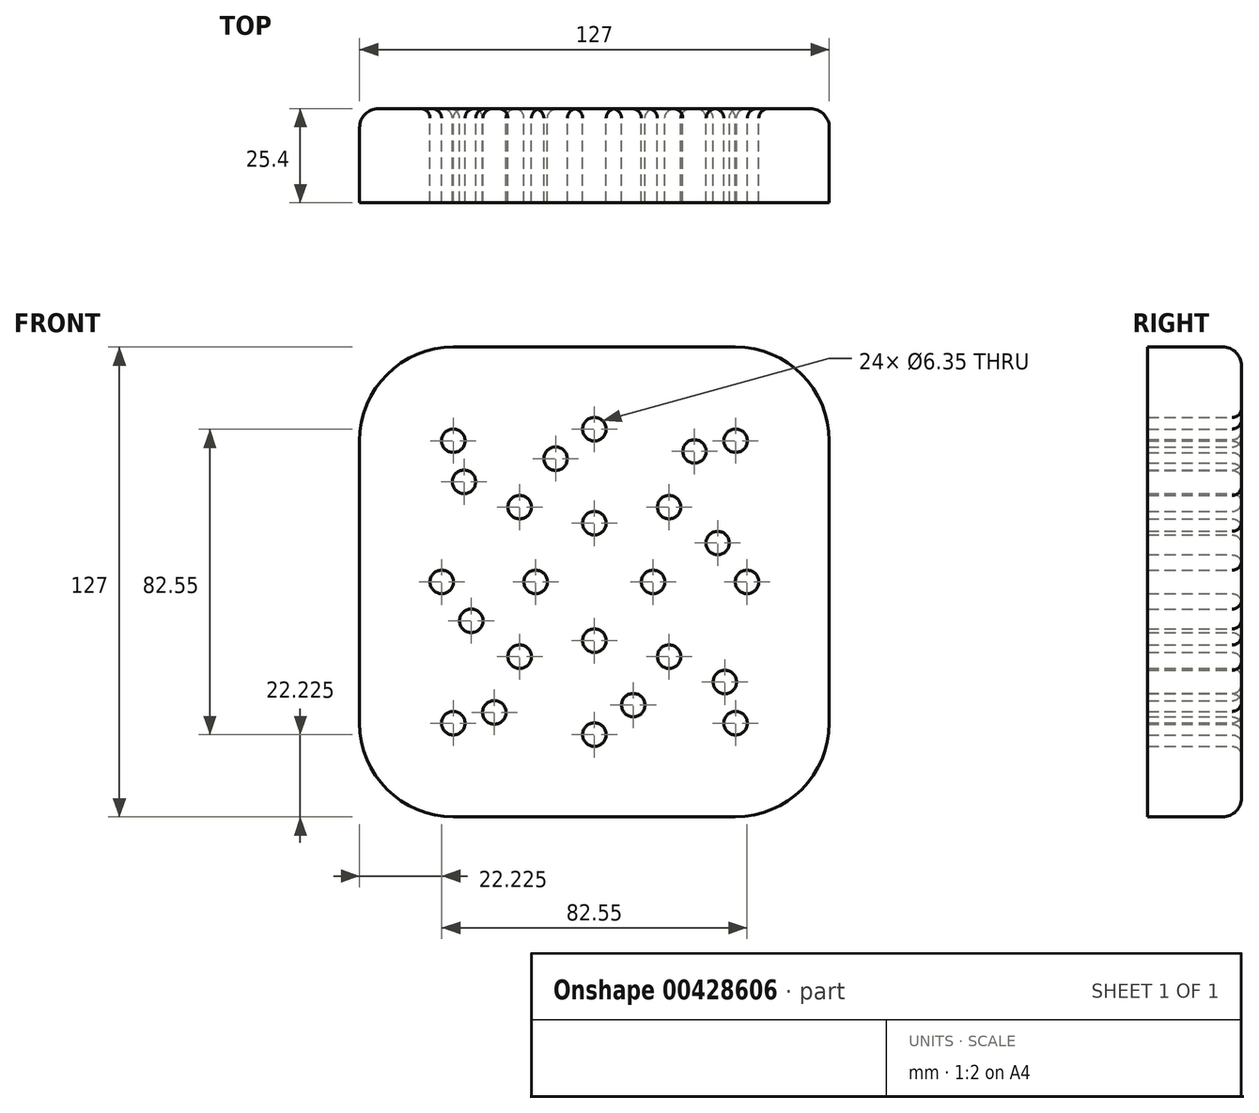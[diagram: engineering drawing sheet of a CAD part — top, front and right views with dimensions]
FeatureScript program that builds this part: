
annotation { "Feature Type Name" : "Feature", "Feature Type Description" : "" }
export const myFeature = defineFeature(function(context is Context, id is Id, definition is map)
    precondition{}
    {
        {
            var Q0;
            Q0=qCreatedBy(makeId("Front.planeOp"),FACE);
            var sketch = newSketch(context, id + "F0", { "sketchPlane" : qUnion([Q0])});
            skCircle(sketch, "E0", {"center": v(0, 0) * mm, "radius": 41.28 * mm, "construction": true});
            skCircle(sketch, "E1", {"center": v(0, -41.27) * mm, "radius": 3.18 * mm});
            skCircle(sketch, "E2", {"center": v(0, 41.28) * mm, "radius": 3.18 * mm});
            skCircle(sketch, "E3", {"center": v(41.27, 0) * mm, "radius": 3.18 * mm});
            skCircle(sketch, "E4", {"center": v(-41.27, 0) * mm, "radius": 3.18 * mm});
            skLineSegment(sketch, "E5", {"start": v(-41.28, 0) * mm, "end": v(0, -41.27) * mm, "construction": true});
            skLineSegment(sketch, "E6", {"start": v(0, -41.27) * mm, "end": v(41.28, 0) * mm, "construction": true});
            skLineSegment(sketch, "E7", {"start": v(41.28, 0) * mm, "end": v(0, 41.28) * mm, "construction": true});
            skLineSegment(sketch, "E8", {"start": v(0, 41.28) * mm, "end": v(-41.27, 0) * mm, "construction": true});
            skLineSegment(sketch, "E9.bottom", {"start": v(63.5, -63.5) * mm, "end": v(-63.5, -63.5) * mm});
            skLineSegment(sketch, "E9.top", {"start": v(63.5, 63.5) * mm, "end": v(-63.5, 63.5) * mm});
            skLineSegment(sketch, "E9.left", {"start": v(63.5, -63.5) * mm, "end": v(63.5, 63.5) * mm});
            skLineSegment(sketch, "E9.right", {"start": v(-63.5, -63.5) * mm, "end": v(-63.5, 63.5) * mm});
            skLineSegment(sketch, "E10", {"start": v(63.5, -63.5) * mm, "end": v(-63.5, 63.5) * mm, "construction": true});
            skLineSegment(sketch, "E11", {"start": v(63.5, 63.5) * mm, "end": v(-63.5, -63.5) * mm, "construction": true});
            skCircle(sketch, "E12", {"center": v(0, 0) * mm, "radius": 53.98 * mm, "construction": true});
            skCircle(sketch, "E13", {"center": v(-38.17, -38.17) * mm, "radius": 3.18 * mm});
            skCircle(sketch, "E14", {"center": v(-38.17, 38.17) * mm, "radius": 3.18 * mm});
            skCircle(sketch, "E15", {"center": v(38.17, 38.17) * mm, "radius": 3.18 * mm});
            skCircle(sketch, "E16", {"center": v(38.17, -38.17) * mm, "radius": 3.18 * mm});
            skLineSegment(sketch, "E17", {"start": v(-38.17, -38.17) * mm, "end": v(-38.17, 38.17) * mm, "construction": true});
            skLineSegment(sketch, "E18", {"start": v(-38.17, 38.17) * mm, "end": v(38.17, 38.17) * mm, "construction": true});
            skLineSegment(sketch, "E19", {"start": v(38.17, 38.17) * mm, "end": v(38.17, -38.17) * mm, "construction": true});
            skLineSegment(sketch, "E20", {"start": v(38.17, -38.17) * mm, "end": v(-38.17, -38.17) * mm, "construction": true});
            skCircle(sketch, "E21", {"center": v(0, 0) * mm, "radius": 28.58 * mm, "construction": true});
            skCircle(sketch, "E22", {"center": v(-20.2, -20.2) * mm, "radius": 3.18 * mm});
            skCircle(sketch, "E23", {"center": v(-20.2, 20.2) * mm, "radius": 3.18 * mm});
            skCircle(sketch, "E24", {"center": v(20.2, 20.2) * mm, "radius": 3.18 * mm});
            skCircle(sketch, "E25", {"center": v(20.2, -20.2) * mm, "radius": 3.18 * mm});
            skLineSegment(sketch, "E26", {"start": v(-20.2, -20.2) * mm, "end": v(-20.2, 20.2) * mm, "construction": true});
            skLineSegment(sketch, "E27", {"start": v(-20.2, 20.2) * mm, "end": v(20.2, 20.2) * mm, "construction": true});
            skLineSegment(sketch, "E28", {"start": v(20.2, 20.2) * mm, "end": v(20.2, -20.2) * mm, "construction": true});
            skLineSegment(sketch, "E29", {"start": v(20.2, -20.2) * mm, "end": v(-20.2, -20.2) * mm, "construction": true});
            skCircle(sketch, "E30", {"center": v(0, 0) * mm, "radius": 15.88 * mm, "construction": true});
            skCircle(sketch, "E31", {"center": v(0, -15.87) * mm, "radius": 3.18 * mm});
            skCircle(sketch, "E32", {"center": v(-15.88, 0) * mm, "radius": 3.17 * mm});
            skCircle(sketch, "E33", {"center": v(0, 15.88) * mm, "radius": 3.17 * mm});
            skCircle(sketch, "E34", {"center": v(15.88, 0) * mm, "radius": 3.17 * mm});
            skLineSegment(sketch, "E35", {"start": v(0, -15.87) * mm, "end": v(-15.88, 0) * mm, "construction": true});
            skLineSegment(sketch, "E36", {"start": v(-15.88, 0) * mm, "end": v(0, 15.88) * mm, "construction": true});
            skLineSegment(sketch, "E37", {"start": v(0, 15.88) * mm, "end": v(15.87, 0) * mm, "construction": true});
            skLineSegment(sketch, "E38", {"start": v(15.87, 0) * mm, "end": v(0, -15.88) * mm, "construction": true});
            skCircle(sketch, "E39", {"center": v(0, 0) * mm, "radius": 44.45 * mm, "construction": true});
            skCircle(sketch, "E40", {"center": v(-27.06, -35.26) * mm, "radius": 3.18 * mm});
            skCircle(sketch, "E41", {"center": v(-35.26, 27.06) * mm, "radius": 3.17 * mm});
            skCircle(sketch, "E42", {"center": v(27.06, 35.26) * mm, "radius": 3.17 * mm});
            skCircle(sketch, "E43", {"center": v(35.26, -27.06) * mm, "radius": 3.17 * mm});
            skLineSegment(sketch, "E44", {"start": v(-27.06, -35.26) * mm, "end": v(-35.26, 27.06) * mm, "construction": true});
            skLineSegment(sketch, "E45", {"start": v(-35.26, 27.06) * mm, "end": v(27.06, 35.26) * mm, "construction": true});
            skLineSegment(sketch, "E46", {"start": v(27.06, 35.26) * mm, "end": v(35.26, -27.06) * mm, "construction": true});
            skLineSegment(sketch, "E47", {"start": v(35.26, -27.06) * mm, "end": v(-27.06, -35.26) * mm, "construction": true});
            skCircle(sketch, "E48", {"center": v(0, 0) * mm, "radius": 34.93 * mm, "construction": true});
            skCircle(sketch, "E49", {"center": v(-33.3, -10.5) * mm, "radius": 3.18 * mm});
            skCircle(sketch, "E50", {"center": v(-10.5, 33.3) * mm, "radius": 3.17 * mm});
            skCircle(sketch, "E51", {"center": v(33.3, 10.5) * mm, "radius": 3.17 * mm});
            skCircle(sketch, "E52", {"center": v(10.5, -33.3) * mm, "radius": 3.17 * mm});
            skLineSegment(sketch, "E53", {"start": v(-33.3, -10.5) * mm, "end": v(-10.5, 33.3) * mm, "construction": true});
            skLineSegment(sketch, "E54", {"start": v(-10.5, 33.3) * mm, "end": v(33.3, 10.5) * mm, "construction": true});
            skLineSegment(sketch, "E55", {"start": v(33.3, 10.5) * mm, "end": v(10.5, -33.3) * mm, "construction": true});
            skLineSegment(sketch, "E56", {"start": v(10.5, -33.3) * mm, "end": v(-33.3, -10.5) * mm, "construction": true});
            skSolve(sketch);
        }
        {
            var Q0;
            Q0=makeQuery(id+"F0.imprint","IMPRINT",FACE,{"disambiguationData":[TD([[makeQuery(id+"F0.imprint","IMPRINT",EDGE,{"derivedFrom":sQuery(id+"F0.wireOp",EDGE,"E1")}),-1.0]])]});
            extrude(context, id + "F1", {"entities" : qUnion([Q0]), "depth" : 25.4 * mm});
        }
        {
            var Q0;
            Q0=makeQuery(id+"F1.opExtrude","SWEPT_EDGE",EDGE,{"disambiguationData":[OSD([sQuery(id+"F0.wireOp",EDGE,"E9.bottom"),sQuery(id+"F0.wireOp",EDGE,"E9.right")])]});
            var Q1;
            Q1=makeQuery(id+"F1.opExtrude","SWEPT_EDGE",EDGE,{"disambiguationData":[OSD([sQuery(id+"F0.wireOp",EDGE,"E9.top"),sQuery(id+"F0.wireOp",EDGE,"E9.right")])]});
            var Q2;
            Q2=makeQuery(id+"F1.opExtrude","SWEPT_EDGE",EDGE,{"disambiguationData":[OSD([sQuery(id+"F0.wireOp",EDGE,"E9.top"),sQuery(id+"F0.wireOp",EDGE,"E9.left")])]});
            var Q3;
            Q3=makeQuery(id+"F1.opExtrude","SWEPT_EDGE",EDGE,{"disambiguationData":[OSD([sQuery(id+"F0.wireOp",EDGE,"E9.bottom"),sQuery(id+"F0.wireOp",EDGE,"E9.left")])]});
            fillet(context, id + "F2", {"entities" : qUnion([Q0, Q1, Q2, Q3]), "radius" : 25.4 * mm, "tangentPropagation" : true, "allowEdgeOverflow" : false});
        }
        {
            var Q0;
            {var subQ0=sQuery(id+"F0.wireOp",EDGE,"E9.right");var subQ1=sQuery(id+"F0.wireOp",EDGE,"E9.bottom");Q0=makeQuery(id+"F2.opFillet","BLEND_EDGE",EDGE,{"blendedFrom":[makeQuery(id+"F1.opExtrude","SWEPT_EDGE",EDGE,{"disambiguationData":[OSD([subQ1,subQ0])]}),makeQuery(id+"F1.opExtrude","CAP_FACE",FACE,{"disambiguationData":[OSD([sQuery(id+"F0.wireOp",EDGE,"E1"),sQuery(id+"F0.wireOp",EDGE,"E2"),sQuery(id+"F0.wireOp",EDGE,"E3"),sQuery(id+"F0.wireOp",EDGE,"E4"),subQ1,sQuery(id+"F0.wireOp",EDGE,"E9.top"),sQuery(id+"F0.wireOp",EDGE,"E9.left"),subQ0,sQuery(id+"F0.wireOp",EDGE,"E13"),sQuery(id+"F0.wireOp",EDGE,"E14"),sQuery(id+"F0.wireOp",EDGE,"E15"),sQuery(id+"F0.wireOp",EDGE,"E16"),sQuery(id+"F0.wireOp",EDGE,"E22"),sQuery(id+"F0.wireOp",EDGE,"E23"),sQuery(id+"F0.wireOp",EDGE,"E24"),sQuery(id+"F0.wireOp",EDGE,"E25"),sQuery(id+"F0.wireOp",EDGE,"E31"),sQuery(id+"F0.wireOp",EDGE,"E32"),sQuery(id+"F0.wireOp",EDGE,"E33"),sQuery(id+"F0.wireOp",EDGE,"E34"),sQuery(id+"F0.wireOp",EDGE,"E40"),sQuery(id+"F0.wireOp",EDGE,"E41"),sQuery(id+"F0.wireOp",EDGE,"E42"),sQuery(id+"F0.wireOp",EDGE,"E43"),sQuery(id+"F0.wireOp",EDGE,"E49"),sQuery(id+"F0.wireOp",EDGE,"E50"),sQuery(id+"F0.wireOp",EDGE,"E51"),sQuery(id+"F0.wireOp",EDGE,"E52")])],"isStart":true})],"blendedInto":[makeQuery(id+"F1.opExtrude","CAP_FACE",FACE,{"disambiguationData":[OSD([sQuery(id+"F0.wireOp",EDGE,"E1"),sQuery(id+"F0.wireOp",EDGE,"E2"),sQuery(id+"F0.wireOp",EDGE,"E3"),sQuery(id+"F0.wireOp",EDGE,"E4"),subQ1,sQuery(id+"F0.wireOp",EDGE,"E9.top"),sQuery(id+"F0.wireOp",EDGE,"E9.left"),subQ0,sQuery(id+"F0.wireOp",EDGE,"E13"),sQuery(id+"F0.wireOp",EDGE,"E14"),sQuery(id+"F0.wireOp",EDGE,"E15"),sQuery(id+"F0.wireOp",EDGE,"E16"),sQuery(id+"F0.wireOp",EDGE,"E22"),sQuery(id+"F0.wireOp",EDGE,"E23"),sQuery(id+"F0.wireOp",EDGE,"E24"),sQuery(id+"F0.wireOp",EDGE,"E25"),sQuery(id+"F0.wireOp",EDGE,"E31"),sQuery(id+"F0.wireOp",EDGE,"E32"),sQuery(id+"F0.wireOp",EDGE,"E33"),sQuery(id+"F0.wireOp",EDGE,"E34"),sQuery(id+"F0.wireOp",EDGE,"E40"),sQuery(id+"F0.wireOp",EDGE,"E41"),sQuery(id+"F0.wireOp",EDGE,"E42"),sQuery(id+"F0.wireOp",EDGE,"E43"),sQuery(id+"F0.wireOp",EDGE,"E49"),sQuery(id+"F0.wireOp",EDGE,"E50"),sQuery(id+"F0.wireOp",EDGE,"E51"),sQuery(id+"F0.wireOp",EDGE,"E52")])],"isStart":true})]});}
            var Q1;
            Q1=makeQuery(id+"F1.opExtrude","CAP_EDGE",EDGE,{"disambiguationData":[OSD([sQuery(id+"F0.wireOp",EDGE,"E9.bottom")])],"isStart":true});
            var Q2;
            {var subQ0=sQuery(id+"F0.wireOp",EDGE,"E9.left");var subQ1=sQuery(id+"F0.wireOp",EDGE,"E9.bottom");Q2=makeQuery(id+"F2.opFillet","BLEND_EDGE",EDGE,{"blendedFrom":[makeQuery(id+"F1.opExtrude","SWEPT_EDGE",EDGE,{"disambiguationData":[OSD([subQ1,subQ0])]}),makeQuery(id+"F1.opExtrude","CAP_FACE",FACE,{"disambiguationData":[OSD([sQuery(id+"F0.wireOp",EDGE,"E1"),sQuery(id+"F0.wireOp",EDGE,"E2"),sQuery(id+"F0.wireOp",EDGE,"E3"),sQuery(id+"F0.wireOp",EDGE,"E4"),subQ1,sQuery(id+"F0.wireOp",EDGE,"E9.top"),subQ0,sQuery(id+"F0.wireOp",EDGE,"E9.right"),sQuery(id+"F0.wireOp",EDGE,"E13"),sQuery(id+"F0.wireOp",EDGE,"E14"),sQuery(id+"F0.wireOp",EDGE,"E15"),sQuery(id+"F0.wireOp",EDGE,"E16"),sQuery(id+"F0.wireOp",EDGE,"E22"),sQuery(id+"F0.wireOp",EDGE,"E23"),sQuery(id+"F0.wireOp",EDGE,"E24"),sQuery(id+"F0.wireOp",EDGE,"E25"),sQuery(id+"F0.wireOp",EDGE,"E31"),sQuery(id+"F0.wireOp",EDGE,"E32"),sQuery(id+"F0.wireOp",EDGE,"E33"),sQuery(id+"F0.wireOp",EDGE,"E34"),sQuery(id+"F0.wireOp",EDGE,"E40"),sQuery(id+"F0.wireOp",EDGE,"E41"),sQuery(id+"F0.wireOp",EDGE,"E42"),sQuery(id+"F0.wireOp",EDGE,"E43"),sQuery(id+"F0.wireOp",EDGE,"E49"),sQuery(id+"F0.wireOp",EDGE,"E50"),sQuery(id+"F0.wireOp",EDGE,"E51"),sQuery(id+"F0.wireOp",EDGE,"E52")])],"isStart":true})],"blendedInto":[makeQuery(id+"F1.opExtrude","CAP_FACE",FACE,{"disambiguationData":[OSD([sQuery(id+"F0.wireOp",EDGE,"E1"),sQuery(id+"F0.wireOp",EDGE,"E2"),sQuery(id+"F0.wireOp",EDGE,"E3"),sQuery(id+"F0.wireOp",EDGE,"E4"),subQ1,sQuery(id+"F0.wireOp",EDGE,"E9.top"),subQ0,sQuery(id+"F0.wireOp",EDGE,"E9.right"),sQuery(id+"F0.wireOp",EDGE,"E13"),sQuery(id+"F0.wireOp",EDGE,"E14"),sQuery(id+"F0.wireOp",EDGE,"E15"),sQuery(id+"F0.wireOp",EDGE,"E16"),sQuery(id+"F0.wireOp",EDGE,"E22"),sQuery(id+"F0.wireOp",EDGE,"E23"),sQuery(id+"F0.wireOp",EDGE,"E24"),sQuery(id+"F0.wireOp",EDGE,"E25"),sQuery(id+"F0.wireOp",EDGE,"E31"),sQuery(id+"F0.wireOp",EDGE,"E32"),sQuery(id+"F0.wireOp",EDGE,"E33"),sQuery(id+"F0.wireOp",EDGE,"E34"),sQuery(id+"F0.wireOp",EDGE,"E40"),sQuery(id+"F0.wireOp",EDGE,"E41"),sQuery(id+"F0.wireOp",EDGE,"E42"),sQuery(id+"F0.wireOp",EDGE,"E43"),sQuery(id+"F0.wireOp",EDGE,"E49"),sQuery(id+"F0.wireOp",EDGE,"E50"),sQuery(id+"F0.wireOp",EDGE,"E51"),sQuery(id+"F0.wireOp",EDGE,"E52")])],"isStart":true})]});}
            var Q3;
            Q3=makeQuery(id+"F1.opExtrude","CAP_EDGE",EDGE,{"disambiguationData":[OSD([sQuery(id+"F0.wireOp",EDGE,"E9.left")])],"isStart":true});
            var Q4;
            Q4=makeQuery(id+"F1.opExtrude","CAP_EDGE",EDGE,{"disambiguationData":[OSD([sQuery(id+"F0.wireOp",EDGE,"E9.right")])],"isStart":true});
            var Q5;
            {var subQ0=sQuery(id+"F0.wireOp",EDGE,"E9.right");var subQ1=sQuery(id+"F0.wireOp",EDGE,"E9.top");Q5=makeQuery(id+"F2.opFillet","BLEND_EDGE",EDGE,{"blendedFrom":[makeQuery(id+"F1.opExtrude","SWEPT_EDGE",EDGE,{"disambiguationData":[OSD([subQ1,subQ0])]}),makeQuery(id+"F1.opExtrude","CAP_FACE",FACE,{"disambiguationData":[OSD([sQuery(id+"F0.wireOp",EDGE,"E1"),sQuery(id+"F0.wireOp",EDGE,"E2"),sQuery(id+"F0.wireOp",EDGE,"E3"),sQuery(id+"F0.wireOp",EDGE,"E4"),sQuery(id+"F0.wireOp",EDGE,"E9.bottom"),subQ1,sQuery(id+"F0.wireOp",EDGE,"E9.left"),subQ0,sQuery(id+"F0.wireOp",EDGE,"E13"),sQuery(id+"F0.wireOp",EDGE,"E14"),sQuery(id+"F0.wireOp",EDGE,"E15"),sQuery(id+"F0.wireOp",EDGE,"E16"),sQuery(id+"F0.wireOp",EDGE,"E22"),sQuery(id+"F0.wireOp",EDGE,"E23"),sQuery(id+"F0.wireOp",EDGE,"E24"),sQuery(id+"F0.wireOp",EDGE,"E25"),sQuery(id+"F0.wireOp",EDGE,"E31"),sQuery(id+"F0.wireOp",EDGE,"E32"),sQuery(id+"F0.wireOp",EDGE,"E33"),sQuery(id+"F0.wireOp",EDGE,"E34"),sQuery(id+"F0.wireOp",EDGE,"E40"),sQuery(id+"F0.wireOp",EDGE,"E41"),sQuery(id+"F0.wireOp",EDGE,"E42"),sQuery(id+"F0.wireOp",EDGE,"E43"),sQuery(id+"F0.wireOp",EDGE,"E49"),sQuery(id+"F0.wireOp",EDGE,"E50"),sQuery(id+"F0.wireOp",EDGE,"E51"),sQuery(id+"F0.wireOp",EDGE,"E52")])],"isStart":true})],"blendedInto":[makeQuery(id+"F1.opExtrude","CAP_FACE",FACE,{"disambiguationData":[OSD([sQuery(id+"F0.wireOp",EDGE,"E1"),sQuery(id+"F0.wireOp",EDGE,"E2"),sQuery(id+"F0.wireOp",EDGE,"E3"),sQuery(id+"F0.wireOp",EDGE,"E4"),sQuery(id+"F0.wireOp",EDGE,"E9.bottom"),subQ1,sQuery(id+"F0.wireOp",EDGE,"E9.left"),subQ0,sQuery(id+"F0.wireOp",EDGE,"E13"),sQuery(id+"F0.wireOp",EDGE,"E14"),sQuery(id+"F0.wireOp",EDGE,"E15"),sQuery(id+"F0.wireOp",EDGE,"E16"),sQuery(id+"F0.wireOp",EDGE,"E22"),sQuery(id+"F0.wireOp",EDGE,"E23"),sQuery(id+"F0.wireOp",EDGE,"E24"),sQuery(id+"F0.wireOp",EDGE,"E25"),sQuery(id+"F0.wireOp",EDGE,"E31"),sQuery(id+"F0.wireOp",EDGE,"E32"),sQuery(id+"F0.wireOp",EDGE,"E33"),sQuery(id+"F0.wireOp",EDGE,"E34"),sQuery(id+"F0.wireOp",EDGE,"E40"),sQuery(id+"F0.wireOp",EDGE,"E41"),sQuery(id+"F0.wireOp",EDGE,"E42"),sQuery(id+"F0.wireOp",EDGE,"E43"),sQuery(id+"F0.wireOp",EDGE,"E49"),sQuery(id+"F0.wireOp",EDGE,"E50"),sQuery(id+"F0.wireOp",EDGE,"E51"),sQuery(id+"F0.wireOp",EDGE,"E52")])],"isStart":true})]});}
            var Q6;
            Q6=makeQuery(id+"F1.opExtrude","CAP_EDGE",EDGE,{"disambiguationData":[OSD([sQuery(id+"F0.wireOp",EDGE,"E9.top")])],"isStart":true});
            var Q7;
            {var subQ0=sQuery(id+"F0.wireOp",EDGE,"E9.left");var subQ1=sQuery(id+"F0.wireOp",EDGE,"E9.top");Q7=makeQuery(id+"F2.opFillet","BLEND_EDGE",EDGE,{"blendedFrom":[makeQuery(id+"F1.opExtrude","SWEPT_EDGE",EDGE,{"disambiguationData":[OSD([subQ1,subQ0])]}),makeQuery(id+"F1.opExtrude","CAP_FACE",FACE,{"disambiguationData":[OSD([sQuery(id+"F0.wireOp",EDGE,"E1"),sQuery(id+"F0.wireOp",EDGE,"E2"),sQuery(id+"F0.wireOp",EDGE,"E3"),sQuery(id+"F0.wireOp",EDGE,"E4"),sQuery(id+"F0.wireOp",EDGE,"E9.bottom"),subQ1,subQ0,sQuery(id+"F0.wireOp",EDGE,"E9.right"),sQuery(id+"F0.wireOp",EDGE,"E13"),sQuery(id+"F0.wireOp",EDGE,"E14"),sQuery(id+"F0.wireOp",EDGE,"E15"),sQuery(id+"F0.wireOp",EDGE,"E16"),sQuery(id+"F0.wireOp",EDGE,"E22"),sQuery(id+"F0.wireOp",EDGE,"E23"),sQuery(id+"F0.wireOp",EDGE,"E24"),sQuery(id+"F0.wireOp",EDGE,"E25"),sQuery(id+"F0.wireOp",EDGE,"E31"),sQuery(id+"F0.wireOp",EDGE,"E32"),sQuery(id+"F0.wireOp",EDGE,"E33"),sQuery(id+"F0.wireOp",EDGE,"E34"),sQuery(id+"F0.wireOp",EDGE,"E40"),sQuery(id+"F0.wireOp",EDGE,"E41"),sQuery(id+"F0.wireOp",EDGE,"E42"),sQuery(id+"F0.wireOp",EDGE,"E43"),sQuery(id+"F0.wireOp",EDGE,"E49"),sQuery(id+"F0.wireOp",EDGE,"E50"),sQuery(id+"F0.wireOp",EDGE,"E51"),sQuery(id+"F0.wireOp",EDGE,"E52")])],"isStart":true})],"blendedInto":[makeQuery(id+"F1.opExtrude","CAP_FACE",FACE,{"disambiguationData":[OSD([sQuery(id+"F0.wireOp",EDGE,"E1"),sQuery(id+"F0.wireOp",EDGE,"E2"),sQuery(id+"F0.wireOp",EDGE,"E3"),sQuery(id+"F0.wireOp",EDGE,"E4"),sQuery(id+"F0.wireOp",EDGE,"E9.bottom"),subQ1,subQ0,sQuery(id+"F0.wireOp",EDGE,"E9.right"),sQuery(id+"F0.wireOp",EDGE,"E13"),sQuery(id+"F0.wireOp",EDGE,"E14"),sQuery(id+"F0.wireOp",EDGE,"E15"),sQuery(id+"F0.wireOp",EDGE,"E16"),sQuery(id+"F0.wireOp",EDGE,"E22"),sQuery(id+"F0.wireOp",EDGE,"E23"),sQuery(id+"F0.wireOp",EDGE,"E24"),sQuery(id+"F0.wireOp",EDGE,"E25"),sQuery(id+"F0.wireOp",EDGE,"E31"),sQuery(id+"F0.wireOp",EDGE,"E32"),sQuery(id+"F0.wireOp",EDGE,"E33"),sQuery(id+"F0.wireOp",EDGE,"E34"),sQuery(id+"F0.wireOp",EDGE,"E40"),sQuery(id+"F0.wireOp",EDGE,"E41"),sQuery(id+"F0.wireOp",EDGE,"E42"),sQuery(id+"F0.wireOp",EDGE,"E43"),sQuery(id+"F0.wireOp",EDGE,"E49"),sQuery(id+"F0.wireOp",EDGE,"E50"),sQuery(id+"F0.wireOp",EDGE,"E51"),sQuery(id+"F0.wireOp",EDGE,"E52")])],"isStart":true})]});}
            fillet(context, id + "F3", {"entities" : qUnion([Q0, Q1, Q2, Q3, Q4, Q5, Q6, Q7]), "radius" : 5.08 * mm, "tangentPropagation" : true, "allowEdgeOverflow" : false});
        }
        {
            var Q0;
            Q0=makeQuery(id+"F1.opExtrude","CAP_EDGE",EDGE,{"disambiguationData":[OSD([sQuery(id+"F0.wireOp",EDGE,"E13")])],"isStart":true});
            var Q1;
            Q1=makeQuery(id+"F1.opExtrude","CAP_EDGE",EDGE,{"disambiguationData":[OSD([sQuery(id+"F0.wireOp",EDGE,"E40")])],"isStart":true});
            var Q2;
            Q2=makeQuery(id+"F1.opExtrude","CAP_EDGE",EDGE,{"disambiguationData":[OSD([sQuery(id+"F0.wireOp",EDGE,"E1")])],"isStart":true});
            var Q3;
            Q3=makeQuery(id+"F1.opExtrude","CAP_EDGE",EDGE,{"disambiguationData":[OSD([sQuery(id+"F0.wireOp",EDGE,"E52")])],"isStart":true});
            var Q4;
            Q4=makeQuery(id+"F1.opExtrude","CAP_EDGE",EDGE,{"disambiguationData":[OSD([sQuery(id+"F0.wireOp",EDGE,"E16")])],"isStart":true});
            var Q5;
            Q5=makeQuery(id+"F1.opExtrude","CAP_EDGE",EDGE,{"disambiguationData":[OSD([sQuery(id+"F0.wireOp",EDGE,"E43")])],"isStart":true});
            var Q6;
            Q6=makeQuery(id+"F1.opExtrude","CAP_EDGE",EDGE,{"disambiguationData":[OSD([sQuery(id+"F0.wireOp",EDGE,"E25")])],"isStart":true});
            var Q7;
            Q7=makeQuery(id+"F1.opExtrude","CAP_EDGE",EDGE,{"disambiguationData":[OSD([sQuery(id+"F0.wireOp",EDGE,"E31")])],"isStart":true});
            var Q8;
            Q8=makeQuery(id+"F1.opExtrude","CAP_EDGE",EDGE,{"disambiguationData":[OSD([sQuery(id+"F0.wireOp",EDGE,"E22")])],"isStart":true});
            var Q9;
            Q9=makeQuery(id+"F1.opExtrude","CAP_EDGE",EDGE,{"disambiguationData":[OSD([sQuery(id+"F0.wireOp",EDGE,"E49")])],"isStart":true});
            var Q10;
            Q10=makeQuery(id+"F1.opExtrude","CAP_EDGE",EDGE,{"disambiguationData":[OSD([sQuery(id+"F0.wireOp",EDGE,"E4")])],"isStart":true});
            var Q11;
            Q11=makeQuery(id+"F1.opExtrude","CAP_EDGE",EDGE,{"disambiguationData":[OSD([sQuery(id+"F0.wireOp",EDGE,"E32")])],"isStart":true});
            var Q12;
            Q12=makeQuery(id+"F1.opExtrude","CAP_EDGE",EDGE,{"disambiguationData":[OSD([sQuery(id+"F0.wireOp",EDGE,"E34")])],"isStart":true});
            var Q13;
            Q13=makeQuery(id+"F1.opExtrude","CAP_EDGE",EDGE,{"disambiguationData":[OSD([sQuery(id+"F0.wireOp",EDGE,"E3")])],"isStart":true});
            var Q14;
            Q14=makeQuery(id+"F1.opExtrude","CAP_EDGE",EDGE,{"disambiguationData":[OSD([sQuery(id+"F0.wireOp",EDGE,"E51")])],"isStart":true});
            var Q15;
            Q15=makeQuery(id+"F1.opExtrude","CAP_EDGE",EDGE,{"disambiguationData":[OSD([sQuery(id+"F0.wireOp",EDGE,"E24")])],"isStart":true});
            var Q16;
            Q16=makeQuery(id+"F1.opExtrude","CAP_EDGE",EDGE,{"disambiguationData":[OSD([sQuery(id+"F0.wireOp",EDGE,"E42")])],"isStart":true});
            var Q17;
            Q17=makeQuery(id+"F1.opExtrude","CAP_EDGE",EDGE,{"disambiguationData":[OSD([sQuery(id+"F0.wireOp",EDGE,"E15")])],"isStart":true});
            var Q18;
            Q18=makeQuery(id+"F1.opExtrude","CAP_EDGE",EDGE,{"disambiguationData":[OSD([sQuery(id+"F0.wireOp",EDGE,"E33")])],"isStart":true});
            var Q19;
            Q19=makeQuery(id+"F1.opExtrude","CAP_EDGE",EDGE,{"disambiguationData":[OSD([sQuery(id+"F0.wireOp",EDGE,"E50")])],"isStart":true});
            var Q20;
            Q20=makeQuery(id+"F1.opExtrude","CAP_EDGE",EDGE,{"disambiguationData":[OSD([sQuery(id+"F0.wireOp",EDGE,"E2")])],"isStart":true});
            var Q21;
            Q21=makeQuery(id+"F1.opExtrude","CAP_EDGE",EDGE,{"disambiguationData":[OSD([sQuery(id+"F0.wireOp",EDGE,"E23")])],"isStart":true});
            var Q22;
            Q22=makeQuery(id+"F1.opExtrude","CAP_EDGE",EDGE,{"disambiguationData":[OSD([sQuery(id+"F0.wireOp",EDGE,"E41")])],"isStart":true});
            var Q23;
            Q23=makeQuery(id+"F1.opExtrude","CAP_EDGE",EDGE,{"disambiguationData":[OSD([sQuery(id+"F0.wireOp",EDGE,"E14")])],"isStart":true});
            fillet(context, id + "F4", {"entities" : qUnion([Q0, Q1, Q2, Q3, Q4, Q5, Q6, Q7, Q8, Q9, Q10, Q11, Q12, Q13, Q14, Q15, Q16, Q17, Q18, Q19, Q20, Q21, Q22, Q23]), "radius" : 2.54 * mm, "tangentPropagation" : true, "allowEdgeOverflow" : false});
        }
    });
